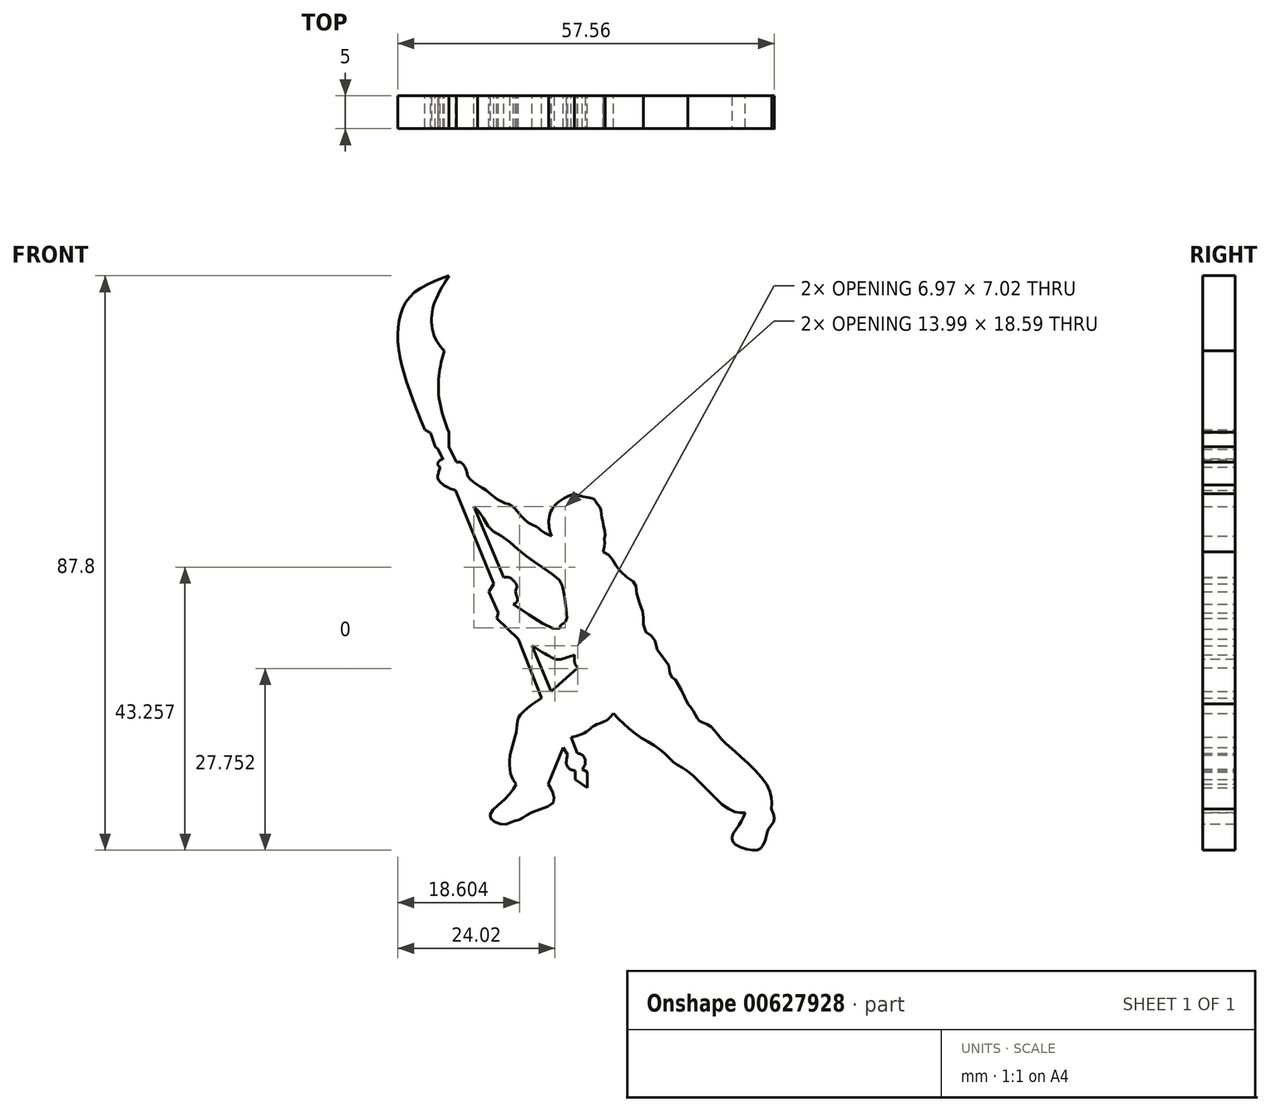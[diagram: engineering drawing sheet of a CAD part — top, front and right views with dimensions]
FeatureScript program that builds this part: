
annotation { "Feature Type Name" : "Feature", "Feature Type Description" : "" }
export const myFeature = defineFeature(function(context is Context, id is Id, definition is map)
    precondition{}
    {
        {
            var Q0;
            Q0=qCreatedBy(makeId("Front.planeOp"),FACE);
            var sketch = newSketch(context, id + "F0", { "sketchPlane" : qUnion([Q0])});
            skLineSegment(sketch, "E0", {"start": v(-18.28, 7.73) * mm, "end": v(-24.12, 21.98) * mm});
            skFitSpline(sketch, "E1", {"points": [v(-24.12, 21.98) * mm, v(-25.46, 22.5) * mm, v(-26.83, 23.73) * mm, v(-26.79, 24.62) * mm, v(-26.52, 25.55) * mm], "startDerivative": vector(-4.76, 1.47) * mm, "endDerivative": vector(1.22, 4.28) * mm});
            skFitSpline(sketch, "E2", {"points": [v(-26.52, 25.55) * mm, v(-26.86, 25.97) * mm, v(-26.52, 26.63) * mm, v(-26.05, 26.73) * mm], "startDerivative": vector(-1.52, 1.09) * mm, "endDerivative": vector(1.57, -0.05) * mm});
            skLineSegment(sketch, "E3", {"start": v(-26.05, 26.73) * mm, "end": v(-26.79, 28.28) * mm});
            skLineSegment(sketch, "E4", {"start": v(-26.79, 28.28) * mm, "end": v(-27.28, 28.7) * mm});
            skLineSegment(sketch, "E5", {"start": v(-27.28, 28.7) * mm, "end": v(-27.94, 30.76) * mm});
            skLineSegment(sketch, "E6", {"start": v(-27.94, 30.76) * mm, "end": v(-28.85, 31.27) * mm});
            skFitSpline(sketch, "E7", {"points": [v(-28.85, 31.27) * mm, v(-32.48, 41.55) * mm, v(-32.83, 47.62) * mm, v(-30.84, 51.88) * mm, v(-25.18, 54.8) * mm], "startDerivative": vector(-13.87, 34.35) * mm, "endDerivative": vector(26.8, 9.95) * mm});
            skFitSpline(sketch, "E8", {"points": [v(-25.18, 54.8) * mm, v(-27.28, 50.9) * mm, v(-27.81, 48.08) * mm, v(-27.28, 45.28) * mm, v(-25.83, 43.33) * mm], "startDerivative": vector(-8.2, -13.54) * mm, "endDerivative": vector(7.45, -8.01) * mm});
            skFitSpline(sketch, "E9", {"points": [v(-25.83, 43.33) * mm, v(-26.6, 40.2) * mm, v(-26.6, 35.72) * mm, v(-25.18, 30.91) * mm], "startDerivative": vector(-3.06, -10.2) * mm, "endDerivative": vector(4.8, -13.1) * mm});
            skLineSegment(sketch, "E10", {"start": v(-25.18, 30.91) * mm, "end": v(-25.18, 28.65) * mm});
            skLineSegment(sketch, "E11", {"start": v(-25.18, 28.65) * mm, "end": v(-24.02, 26.3) * mm});
            skFitSpline(sketch, "E12", {"points": [v(-24.02, 26.3) * mm, v(-23.44, 26.3) * mm, v(-22.94, 25.92) * mm, v(-22.39, 24.75) * mm, v(-22.27, 24.17) * mm, v(-21.75, 23.56) * mm, v(-20.78, 22.83) * mm], "startDerivative": vector(4.33, 0.48) * mm, "endDerivative": vector(5.02, -3.59) * mm});
            skFitSpline(sketch, "E13", {"points": [v(-20.78, 22.83) * mm, v(-19.46, 21.98) * mm, v(-17.06, 20.24) * mm, v(-15.43, 19.55) * mm, v(-13.37, 17.3) * mm, v(-11.4, 16.22) * mm, v(-10.97, 15.77) * mm, v(-9.5, 14.99) * mm], "startDerivative": vector(9.3, -5.33) * mm, "endDerivative": vector(13.24, -5.98) * mm});
            skFitSpline(sketch, "E14", {"points": [v(-9.5, 14.99) * mm, v(-9.8, 16.2) * mm, v(-9.84, 18) * mm, v(-8.59, 20.08) * mm, v(-6.02, 21.5) * mm], "startDerivative": vector(-1.71, 5.86) * mm, "endDerivative": vector(9.37, 3.98) * mm});
            skFitSpline(sketch, "E15", {"points": [v(-6.02, 21.5) * mm, v(-5.71, 21.34) * mm, v(-5.07, 21.15) * mm, v(-3.46, 20.83) * mm, v(-2.97, 20.64) * mm, v(-2.7, 20.26) * mm, v(-2.64, 20.09) * mm, v(-2.3, 19.69) * mm, v(-1.96, 19.17) * mm, v(-1.8, 17.97) * mm, v(-1.69, 17.33) * mm, v(-1.3, 15.47) * mm, v(-1.3, 14.99) * mm, v(-1.42, 14.7) * mm, v(-1.34, 13.73) * mm, v(-1.58, 12.84) * mm, v(-1.6, 12.6) * mm], "startDerivative": vector(6.36, -3.86) * mm, "endDerivative": vector(0.14, -5.52) * mm});
            skFitSpline(sketch, "E16", {"points": [v(-1.6, 12.6) * mm, v(-0.63, 12.03) * mm, v(0, 11.08) * mm, v(0.82, 9.92) * mm, v(2.22, 8.56) * mm, v(3.3, 7.86) * mm, v(3.46, 6.66) * mm, v(4.2, 4.06) * mm, v(4.57, 2.86) * mm, v(4.58, 1.44) * mm, v(5.26, 0) * mm, v(6.15, -0.53) * mm, v(6.74, -2.5) * mm, v(8.4, -4.7) * mm, v(8.7, -6.32) * mm, v(8.95, -6.57) * mm, v(9.24, -6.71) * mm, v(11.35, -10.64) * mm], "startDerivative": vector(20.98, -9.23) * mm, "endDerivative": vector(24.88, -52.3) * mm});
            skFitSpline(sketch, "E17", {"points": [v(11.35, -10.64) * mm, v(12.42, -12.07) * mm, v(13.1, -13.25) * mm, v(14.48, -13.84) * mm, v(16.25, -15.7) * mm, v(18.5, -17.87) * mm, v(23.61, -23.37) * mm, v(24.1, -26.7) * mm], "startDerivative": vector(10.47, -12.1) * mm, "endDerivative": vector(-1.45, -20.03) * mm});
            skFitSpline(sketch, "E18", {"points": [v(24.1, -26.7) * mm, v(24.54, -28.53) * mm, v(23.68, -29.76) * mm, v(23.31, -30.96) * mm, v(22.53, -32.65) * mm, v(21.2, -32.98) * mm, v(18.44, -32) * mm, v(18.15, -30.75) * mm, v(19.3, -28.98) * mm, v(20.1, -27.24) * mm], "startDerivative": vector(7.58, -16.92) * mm, "endDerivative": vector(5.4, 15.06) * mm});
            skFitSpline(sketch, "E19", {"points": [v(20.1, -27.24) * mm, v(17.56, -26.7) * mm, v(11.78, -21.29) * mm, v(9.39, -19.7) * mm, v(7.17, -17.67) * mm, v(3.32, -15.21) * mm, v(0, -12.07) * mm], "startDerivative": vector(-17.42, -0.71) * mm, "endDerivative": vector(-17.5, 19.05) * mm});
            skFitSpline(sketch, "E20", {"points": [v(0, -12.07) * mm, v(-1.25, -13.26) * mm, v(-2.87, -13.92) * mm, v(-4.36, -15.04) * mm, v(-6.5, -15.74) * mm], "startDerivative": vector(-4.73, -5.73) * mm, "endDerivative": vector(-8.47, -1.85) * mm});
            skLineSegment(sketch, "E21", {"start": v(-6.5, -15.74) * mm, "end": v(-5.51, -18.17) * mm});
            skFitSpline(sketch, "E22", {"points": [v(-5.51, -18.17) * mm, v(-4.69, -18.55) * mm, v(-4.32, -19.62) * mm, v(-4.77, -20.61) * mm], "startDerivative": vector(2.9, -0.7) * mm, "endDerivative": vector(-1.86, -2.73) * mm});
            skLineSegment(sketch, "E23", {"start": v(-4.77, -20.61) * mm, "end": v(-4.03, -21.02) * mm});
            skLineSegment(sketch, "E24", {"start": v(-4.03, -21.02) * mm, "end": v(-4.03, -23.46) * mm});
            skLineSegment(sketch, "E25", {"start": v(-4.03, -23.46) * mm, "end": v(-5.88, -22.18) * mm});
            skLineSegment(sketch, "E26", {"start": v(-5.88, -22.18) * mm, "end": v(-5.88, -20.86) * mm});
            skFitSpline(sketch, "E27", {"points": [v(-5.88, -20.86) * mm, v(-6.8, -20.51) * mm, v(-7.22, -19.75) * mm, v(-7.01, -18.43) * mm], "startDerivative": vector(-3.15, 0.75) * mm, "endDerivative": vector(1.02, 3.7) * mm});
            skLineSegment(sketch, "E28", {"start": v(-7.67, -17.28) * mm, "end": v(-7.01, -18.43) * mm});
            skLineSegment(sketch, "E29", {"start": v(-7.67, -17.28) * mm, "end": v(-10, -22.9) * mm});
            skFitSpline(sketch, "E30", {"points": [v(-10, -22.9) * mm, v(-9.26, -24.32) * mm, v(-9.32, -25.84) * mm, v(-12.82, -27.36) * mm, v(-14.05, -28.17) * mm, v(-15.45, -28.64) * mm, v(-16.68, -29.05) * mm, v(-18.55, -28.4) * mm, v(-18.78, -27.36) * mm, v(-16.33, -24.9) * mm, v(-14.87, -22.9) * mm], "startDerivative": vector(8.86, -14.78) * mm, "endDerivative": vector(10.05, 17.22) * mm});
            skFitSpline(sketch, "E31", {"points": [v(-14.87, -22.9) * mm, v(-15.63, -21.63) * mm, v(-15.8, -18.48) * mm, v(-14.87, -14.86) * mm, v(-14.46, -12.64) * mm, v(-11.01, -9.72) * mm], "startDerivative": vector(-5.97, 7.67) * mm, "endDerivative": vector(17.63, 11.7) * mm});
            skLineSegment(sketch, "E32", {"start": v(-11.01, -9.72) * mm, "end": v(-14.59, -0.73) * mm});
            skLineSegment(sketch, "E33", {"start": v(-14.59, -0.73) * mm, "end": v(-17.83, 2.42) * mm});
            skLineSegment(sketch, "E34", {"start": v(-17.83, 2.42) * mm, "end": v(-17.58, 3.25) * mm});
            skLineSegment(sketch, "E35", {"start": v(-17.58, 3.25) * mm, "end": v(-19.04, 6.51) * mm});
            skLineSegment(sketch, "E36", {"start": v(-19.04, 6.51) * mm, "end": v(-18.28, 7.73) * mm});
            skLineSegment(sketch, "E37", {"start": v(-12.45, -1.74) * mm, "end": v(-9.55, -8.76) * mm});
            skLineSegment(sketch, "E38", {"start": v(-9.55, -8.76) * mm, "end": v(-5.47, -5.13) * mm});
            skFitSpline(sketch, "E39", {"points": [v(-5.47, -5.13) * mm, v(-5.92, -4.44) * mm, v(-5.96, -3.16) * mm], "startDerivative": vector(-1.2, 1.38) * mm, "endDerivative": vector(0.16, 2.5) * mm});
            skFitSpline(sketch, "E40", {"points": [v(-5.96, -3.16) * mm, v(-8.03, -3.8) * mm, v(-8.86, -3.8) * mm, v(-12.45, -1.74) * mm], "startDerivative": vector(-7.07, -2.3) * mm, "endDerivative": vector(-9.27, 5.94) * mm});
            skLineSegment(sketch, "E41", {"start": v(-21.37, 19.55) * mm, "end": v(-16.76, 8.65) * mm});
            skFitSpline(sketch, "E42", {"points": [v(-21.37, 19.55) * mm, v(-20.14, 18.23) * mm, v(-18.92, 16.16) * mm, v(-17, 14.94) * mm, v(-14, 12.48) * mm, v(-11.5, 10.66) * mm, v(-8.46, 8.4) * mm, v(-7.72, 7.13) * mm, v(-7.13, 2.86) * mm, v(-7.28, 1.92) * mm, v(-7.97, 1.53) * mm, v(-8.21, 1) * mm, v(-9.05, 0.84) * mm, v(-15.33, 4.58) * mm], "startDerivative": vector(19.05, -16.82) * mm, "endDerivative": vector(-54.78, 37.42) * mm});
            skFitSpline(sketch, "E43", {"points": [v(-15.33, 4.58) * mm, v(-14.7, 5.21) * mm, v(-14.99, 6.69) * mm, v(-14.74, 7.28) * mm, v(-15.82, 8.65) * mm, v(-16.76, 8.65) * mm], "startDerivative": vector(5, 2.63) * mm, "endDerivative": vector(-4.75, -1.45) * mm});
            skSolve(sketch);
        }
        {
            var Q0;
            Q0 = qSketchRegion(id + "F0", true);
            extrude(context, id + "F1", {"entities" : qUnion([Q0]), "depth" : 5 * mm, "offsetDistance" : 25 * mm});
        }
    });
